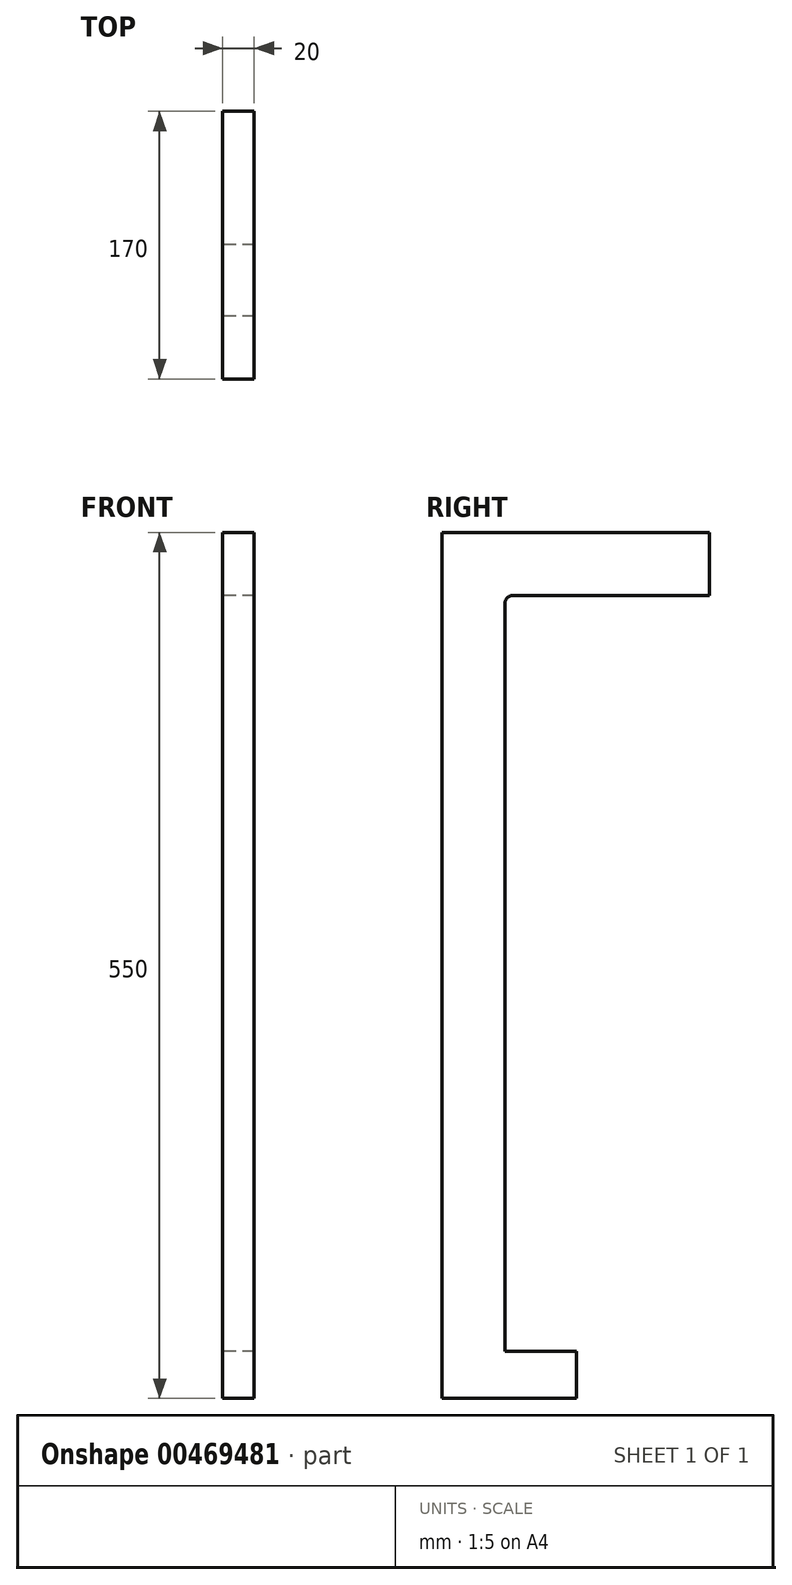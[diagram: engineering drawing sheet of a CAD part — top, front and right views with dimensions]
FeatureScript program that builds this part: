
annotation { "Feature Type Name" : "Feature", "Feature Type Description" : "" }
export const myFeature = defineFeature(function(context is Context, id is Id, definition is map)
    precondition{}
    {
        {
            var Q0;
            Q0=qCreatedBy(makeId("Right.planeOp"),FACE);
            var sketch = newSketch(context, id + "F0", { "sketchPlane" : qUnion([Q0])});
            skLineSegment(sketch, "E0", {"start": v(-40, 0) * mm, "end": v(-40, 550) * mm});
            skLineSegment(sketch, "E1", {"start": v(-40, 550) * mm, "end": v(130, 550) * mm});
            skLineSegment(sketch, "E2", {"start": v(130, 550) * mm, "end": v(130, 510) * mm});
            skLineSegment(sketch, "E3", {"start": v(130, 510) * mm, "end": v(5, 510) * mm});
            skLineSegment(sketch, "E4", {"start": v(0, 505) * mm, "end": v(0, 0) * mm});
            skLineSegment(sketch, "E5", {"start": v(0, 0) * mm, "end": v(-40, 0) * mm});
            skPoint(sketch, "E6.visualSharp", {"position": v(0, 510) * mm});
            skArc(sketch, "E6.filletArc", {"start": v(5, 510) * mm, "mid": v(1.46, 508.54) * mm, "end": v(0, 505) * mm});
            skLineSegment(sketch, "E7.bottom", {"start": v(0, 0) * mm, "end": v(45.37, 0) * mm});
            skLineSegment(sketch, "E7.top", {"start": v(0, 30) * mm, "end": v(45.37, 30) * mm});
            skLineSegment(sketch, "E7.left", {"start": v(0, 0) * mm, "end": v(0, 30) * mm});
            skLineSegment(sketch, "E7.right", {"start": v(45.37, 0) * mm, "end": v(45.37, 30) * mm});
            skSolve(sketch);
        }
        {
            var Q0;
            Q0 = qSketchRegion(id + "F0", true);
            extrude(context, id + "F1", {"entities" : qUnion([Q0]), "depth" : 20 * mm});
        }
    });
